# Revit family: Xbeam - 20m x 8m Platform Base ASSY
name_source: partatom
category: Equipos mecánicos
revit_build: Autodesk Revit 2017 (Build: 20181011_1645(x64)
units: mm (PartAtom-declared; Revit-internal decimal feet)

## family parameters
Anfitrión = Cubierta
Compartido = No
Corte con vacíos al cargar = No
Cota de conector redondo = Diámetro de uso
Punto de cálculo de habitación = No
Siempre vertical = Sí
Tipo de pieza = Normal

## types (1)
- Xbeam - 20m x 8m Platform Base ASSY
    1200mm (1) = Sí
    1500mm (2) = No
    1800mm (3) = No
    2.5kPa (1) = Sí
    2100mm (4) = No
    2400mm (5) = No
    2700mm (6) = No
    3.0kPa (2) = No
    3000mm (7) = No
    5.0kPa (3) = No
    Acoustic Screening Only_A (3) = No
    Handrail_A (5) = No
    Leg length = 1 mm  [stored 0.00328084 ft]
    Louvres and Acoustic Screening_A (2) = No
    Louvres_A (1) = Sí
    Min. Max. Platform Capacity Rating Selection = 1
    Min. Max. Screen Height Selection = 1
    Min. Max. Screen Options = 1
    Perforated Sheet Screens_A (4) = No
    Platform Capacity Rating Selection = 1
    Platform Lenght = 20000 mm  [stored 65.6168 ft]
    Platform Width = 8000 mm  [stored 26.2467 ft]
    Portal Offset = 200 mm  [stored 0.656168 ft]
    Portal spacing = 11000 mm  [stored 36.0892 ft]
    Primary Bearer spacing = 8000 mm  [stored 26.2467 ft]
    Screen Extended Below = 500 mm  [stored 1.64042 ft]
    Screen Height Selection = 1
    Screen Options = 1
    Second Portal Spacing = 19000 mm
    Secondary Bearer spacing = 1200 mm

note: [stored X ft] marks values corroborated as IEEE doubles in the binary element streams (Revit-internal decimal feet)

## geometry (parser evidence)
native form markers: Sweep x25
no freeform markers — native parametric forms only
